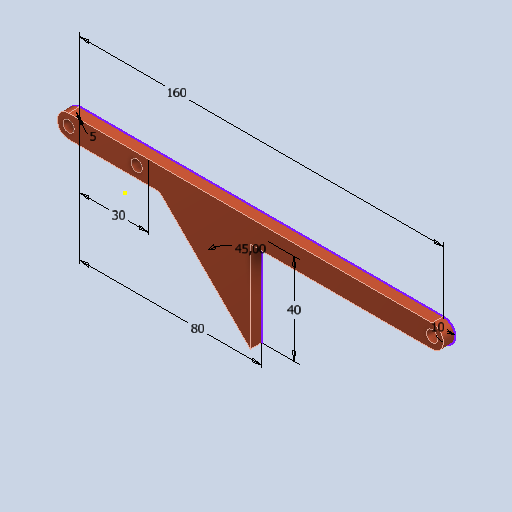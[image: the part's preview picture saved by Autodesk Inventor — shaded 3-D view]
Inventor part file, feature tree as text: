
AUTODESK INVENTOR PART (.ipt)
format: ipt  version: 2022 (Build 260153000, 153)  size: 118,272 bytes
history: native  units: mm
features: extrude x3, sketch x1
ambient origin geometry x8: Origin, YZ Plane, XZ Plane, XY Plane, X Axis, Y Axis, Z Axis, Center Point
bodies: Solid1 (feature_tree)
feature tree (4):
  sketch  "Sketch1"  dims[d0=10.0mm d1=5.0mm d2=160.0mm d3=5.0mm d4=0.0mm d7=30.0mm d8=10.0mm d9=0.0mm d10=45.0deg d11=40.0mm d12=80.0mm d13=10.0mm d14=0.0mm]
  extrude  "Extrusion1"  Depth=5.0mm
  extrude  "Extrusion3"  Depth=10.0mm
  extrude  "Extrusion4"  Depth=5.0mm TaperAngle=0.0deg
